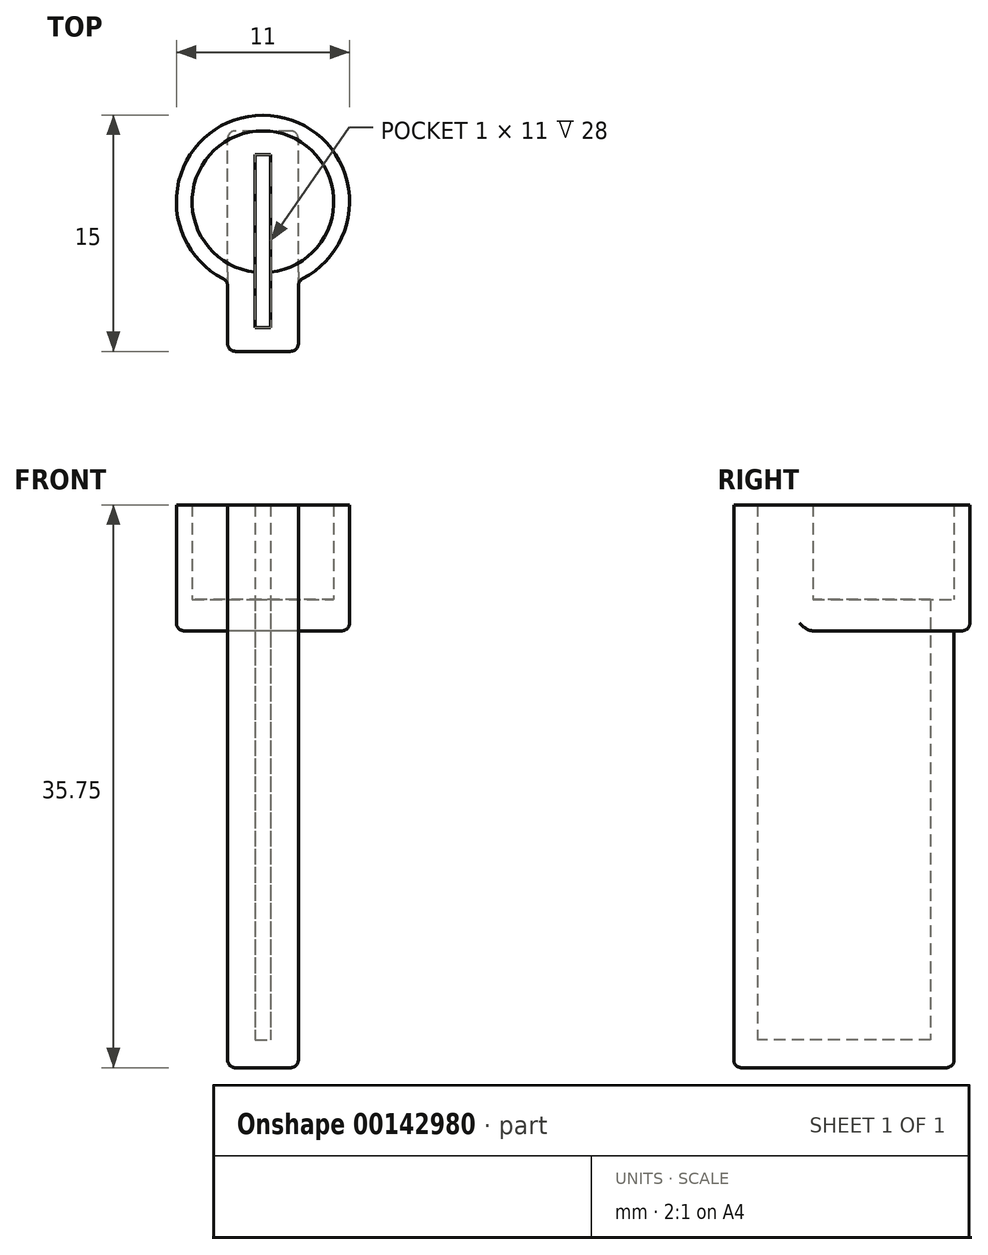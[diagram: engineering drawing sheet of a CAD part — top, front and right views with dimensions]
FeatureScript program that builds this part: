
annotation { "Feature Type Name" : "Feature", "Feature Type Description" : "" }
export const myFeature = defineFeature(function(context is Context, id is Id, definition is map)
    precondition{}
    {
        {
            var Q0;
            Q0=qCreatedBy(makeId("Top.planeOp"),FACE);
            var sketch = newSketch(context, id + "F0", { "sketchPlane" : qUnion([Q0])});
            skLineSegment(sketch, "E0.bottom", {"start": v(2.25, -7) * mm, "end": v(-2.25, -7) * mm});
            skLineSegment(sketch, "E0.top", {"start": v(2.25, 7) * mm, "end": v(-2.25, 7) * mm});
            skLineSegment(sketch, "E0.left", {"start": v(2.25, -7) * mm, "end": v(2.25, 7) * mm});
            skLineSegment(sketch, "E0.right", {"start": v(-2.25, -7) * mm, "end": v(-2.25, 7) * mm});
            skPoint(sketch, "E0.middle", {"position": v(0, 0) * mm});
            skSolve(sketch);
        }
        {
            var Q0;
            Q0 = qSketchRegion(id + "F0", true);
            extrude(context, id + "F1", {"entities" : qUnion([Q0]), "depth" : 1.75 * mm});
        }
        {
            var Q0;
            Q0=makeQuery(id+"F1.opExtrude","CAP_FACE",FACE,{"disambiguationData":[OSD([sQuery(id+"F0.wireOp",EDGE,"E0.bottom"),sQuery(id+"F0.wireOp",EDGE,"E0.top"),sQuery(id+"F0.wireOp",EDGE,"E0.left"),sQuery(id+"F0.wireOp",EDGE,"E0.right")])],"isStart":false});
            var sketch = newSketch(context, id + "F2", { "sketchPlane" : qUnion([Q0])});
            skPoint(sketch, "E1.middle", {"position": v(0, 0) * mm});
            skLineSegment(sketch, "E2.bottom", {"start": v(-2.25, 7) * mm, "end": v(2.25, 7) * mm});
            skLineSegment(sketch, "E2.top", {"start": v(-2.25, -7) * mm, "end": v(2.25, -7) * mm});
            skLineSegment(sketch, "E2.left", {"start": v(-2.25, 7) * mm, "end": v(-2.25, -7) * mm});
            skLineSegment(sketch, "E2.right", {"start": v(2.25, 7) * mm, "end": v(2.25, -7) * mm});
            skLineSegment(sketch, "E3.bottom", {"start": v(-0.5, 5.5) * mm, "end": v(0.5, 5.5) * mm});
            skLineSegment(sketch, "E3.top", {"start": v(-0.5, -5.5) * mm, "end": v(0.5, -5.5) * mm});
            skLineSegment(sketch, "E3.left", {"start": v(-0.5, 5.5) * mm, "end": v(-0.5, -5.5) * mm});
            skLineSegment(sketch, "E3.right", {"start": v(0.5, 5.5) * mm, "end": v(0.5, -5.5) * mm});
            skSolve(sketch);
        }
        {
            var Q0;
            Q0 = qSketchRegion(id + "F2", true);
            extrude(context, id + "F3", {"entities" : qUnion([Q0]), "operationType" : NewBodyOperationType.ADD, "depth" : 26 * mm});
        }
        {
            var Q0;
            Q0=makeQuery(id+"F3.opExtrude","CAP_FACE",FACE,{"disambiguationData":[OSD([sQuery(id+"F2.wireOp",EDGE,"E2.bottom"),sQuery(id+"F2.wireOp",EDGE,"E2.top"),sQuery(id+"F2.wireOp",EDGE,"E2.left"),sQuery(id+"F2.wireOp",EDGE,"E2.right"),sQuery(id+"F2.wireOp",EDGE,"E3.bottom"),sQuery(id+"F2.wireOp",EDGE,"E3.top"),sQuery(id+"F2.wireOp",EDGE,"E3.left"),sQuery(id+"F2.wireOp",EDGE,"E3.right")])],"isStart":false});
            var sketch = newSketch(context, id + "F4", { "sketchPlane" : qUnion([Q0])});
            skPoint(sketch, "E4.first.point", {"position": v(-4.26, 6.2) * mm});
            skPoint(sketch, "E4.second.point", {"position": v(4.05, 6.34) * mm});
            skPoint(sketch, "E4.third.point", {"position": v(3.62, -1.7) * mm});
            skLineSegment(sketch, "E5", {"start": v(-2.25, -2.52) * mm, "end": v(-2.25, -7) * mm});
            skLineSegment(sketch, "E6", {"start": v(-2.25, -7) * mm, "end": v(2.25, -7) * mm});
            skLineSegment(sketch, "E7", {"start": v(2.25, -7) * mm, "end": v(2.25, -2.52) * mm});
            skLineSegment(sketch, "E8", {"start": v(0.5, -2.98) * mm, "end": v(0.5, -5.5) * mm});
            skLineSegment(sketch, "E9", {"start": v(0.5, -5.5) * mm, "end": v(0.5, 5.5) * mm});
            skLineSegment(sketch, "E10", {"start": v(0.5, -5.5) * mm, "end": v(-0.5, -5.5) * mm});
            skLineSegment(sketch, "E11", {"start": v(-0.5, -5.5) * mm, "end": v(-0.5, 5.5) * mm});
            skArc(sketch, "E12.trimOffspring", {"start": v(2.25, -2.52) * mm, "mid": v(0, 8) * mm, "end": v(-2.25, -2.52) * mm});
            skLineSegment(sketch, "E13", {"start": v(-0.5, 5.5) * mm, "end": v(0.5, 5.5) * mm});
            skSolve(sketch);
        }
        {
            var Q0;
            Q0 = qSketchRegion(id + "F4", true);
            extrude(context, id + "F5", {"entities" : qUnion([Q0]), "operationType" : NewBodyOperationType.ADD, "depth" : 2 * mm});
        }
        {
            var Q0;
            Q0=makeQuery(id+"F5.opExtrude","CAP_FACE",FACE,{"disambiguationData":[OSD([sQuery(id+"F4.wireOp",EDGE,"E5"),sQuery(id+"F4.wireOp",EDGE,"E6"),sQuery(id+"F4.wireOp",EDGE,"E7"),sQuery(id+"F4.wireOp",EDGE,"E9"),sQuery(id+"F4.wireOp",EDGE,"E10"),sQuery(id+"F4.wireOp",EDGE,"E11"),sQuery(id+"F4.wireOp",EDGE,"E12.trimOffspring"),sQuery(id+"F4.wireOp",EDGE,"E13")])],"isStart":false});
            var sketch = newSketch(context, id + "F6", { "sketchPlane" : qUnion([Q0])});
            skArc(sketch, "E14", {"start": v(2.25, -2.52) * mm, "mid": v(0, 8) * mm, "end": v(-2.25, -2.52) * mm});
            skArc(sketch, "E15", {"start": v(0.5, -1.97) * mm, "mid": v(0, 7) * mm, "end": v(-0.5, -1.97) * mm});
            skLineSegment(sketch, "E16", {"start": v(-0.5, -1.97) * mm, "end": v(-0.5, -5.5) * mm});
            skLineSegment(sketch, "E17", {"start": v(-0.5, -5.5) * mm, "end": v(0.5, -5.5) * mm});
            skLineSegment(sketch, "E18", {"start": v(0.5, -5.5) * mm, "end": v(0.5, -1.97) * mm});
            skLineSegment(sketch, "E19", {"start": v(-2.25, -2.52) * mm, "end": v(-2.25, -7) * mm});
            skLineSegment(sketch, "E20", {"start": v(-2.25, -7) * mm, "end": v(2.25, -7) * mm});
            skLineSegment(sketch, "E21", {"start": v(2.25, -7) * mm, "end": v(2.25, -2.52) * mm});
            skSolve(sketch);
        }
        {
            var Q0;
            Q0 = qSketchRegion(id + "F6", true);
            extrude(context, id + "F7", {"entities" : qUnion([Q0]), "operationType" : NewBodyOperationType.ADD, "depth" : 6 * mm});
        }
        {
            var Q0;
            Q0=makeQuery(id+"F7.boolean.opBoolean","MERGE",EDGE,{"derivedFrom":[makeQuery(id+"F5.opExtrude","SWEPT_EDGE",EDGE,{"disambiguationData":[OSD([sQuery(id+"F2.wireOp",EDGE,"E2.right"),sQuery(id+"F4.wireOp",EDGE,"E7"),sQuery(id+"F4.wireOp",EDGE,"E12.trimOffspring")])]}),makeQuery(id+"F7.opExtrude","SWEPT_EDGE",EDGE,{"disambiguationData":[OSD([sQuery(id+"F6.wireOp",EDGE,"E14"),sQuery(id+"F6.wireOp",EDGE,"E21")])]})]});
            var Q1;
            Q1=makeQuery(id+"F3.opExtrude","CAP_EDGE",EDGE,{"disambiguationData":[OSD([sQuery(id+"F2.wireOp",EDGE,"E2.right")])],"isStart":false});
            var Q2;
            Q2=makeQuery(id+"F3.opExtrude","CAP_EDGE",EDGE,{"disambiguationData":[OSD([sQuery(id+"F2.wireOp",EDGE,"E2.bottom")])],"isStart":false});
            var Q3;
            Q3=makeQuery(id+"F3.opExtrude","CAP_EDGE",EDGE,{"disambiguationData":[OSD([sQuery(id+"F2.wireOp",EDGE,"E2.left")])],"isStart":false});
            var Q4;
            Q4=makeQuery(id+"F7.boolean.opBoolean","MERGE",EDGE,{"derivedFrom":[makeQuery(id+"F5.opExtrude","SWEPT_EDGE",EDGE,{"disambiguationData":[OSD([sQuery(id+"F2.wireOp",EDGE,"E2.left"),sQuery(id+"F4.wireOp",EDGE,"E5"),sQuery(id+"F4.wireOp",EDGE,"E12.trimOffspring")])]}),makeQuery(id+"F7.opExtrude","SWEPT_EDGE",EDGE,{"disambiguationData":[OSD([sQuery(id+"F6.wireOp",EDGE,"E14"),sQuery(id+"F6.wireOp",EDGE,"E19")])]})]});
            fillet(context, id + "F8", {"entities" : qUnion([Q0, Q1, Q2, Q3, Q4]), "radius" : 0.5 * mm, "tangentPropagation" : true, "allowEdgeOverflow" : false});
        }
        {
            var Q0;
            Q0=makeQuery(id+"F5.opExtrude","CAP_EDGE",EDGE,{"disambiguationData":[OSD([sQuery(id+"F4.wireOp",EDGE,"E12.trimOffspring")])],"isStart":true});
            fillet(context, id + "F9", {"entities" : qUnion([Q0]), "radius" : 0.5 * mm, "tangentPropagation" : true, "allowEdgeOverflow" : false});
        }
        {
            var Q0;
            Q0=makeQuery(id+"F7.boolean.opBoolean","MERGE",EDGE,{"derivedFrom":[makeQuery(id+"F5.boolean.opBoolean","MERGE",EDGE,{"derivedFrom":[makeQuery(id+"F3.boolean.opBoolean","MERGE",EDGE,{"derivedFrom":[makeQuery(id+"F1.opExtrude","SWEPT_EDGE",EDGE,{"disambiguationData":[OSD([sQuery(id+"F0.wireOp",EDGE,"E0.bottom"),sQuery(id+"F0.wireOp",EDGE,"E0.right")])]}),makeQuery(id+"F3.opExtrude","SWEPT_EDGE",EDGE,{"disambiguationData":[OSD([sQuery(id+"F2.wireOp",EDGE,"E2.top"),sQuery(id+"F2.wireOp",EDGE,"E2.left")])]})]}),makeQuery(id+"F5.opExtrude","SWEPT_EDGE",EDGE,{"disambiguationData":[OSD([sQuery(id+"F4.wireOp",EDGE,"E5"),sQuery(id+"F4.wireOp",EDGE,"E6")])]})]}),makeQuery(id+"F7.opExtrude","SWEPT_EDGE",EDGE,{"disambiguationData":[OSD([sQuery(id+"F6.wireOp",EDGE,"E19"),sQuery(id+"F6.wireOp",EDGE,"E20")])]})]});
            var Q1;
            Q1=makeQuery(id+"F7.boolean.opBoolean","MERGE",EDGE,{"derivedFrom":[makeQuery(id+"F5.boolean.opBoolean","MERGE",EDGE,{"derivedFrom":[makeQuery(id+"F3.boolean.opBoolean","MERGE",EDGE,{"derivedFrom":[makeQuery(id+"F1.opExtrude","SWEPT_EDGE",EDGE,{"disambiguationData":[OSD([sQuery(id+"F0.wireOp",EDGE,"E0.bottom"),sQuery(id+"F0.wireOp",EDGE,"E0.left")])]}),makeQuery(id+"F3.opExtrude","SWEPT_EDGE",EDGE,{"disambiguationData":[OSD([sQuery(id+"F2.wireOp",EDGE,"E2.top"),sQuery(id+"F2.wireOp",EDGE,"E2.right")])]})]}),makeQuery(id+"F5.opExtrude","SWEPT_EDGE",EDGE,{"disambiguationData":[OSD([sQuery(id+"F4.wireOp",EDGE,"E6"),sQuery(id+"F4.wireOp",EDGE,"E7")])]})]}),makeQuery(id+"F7.opExtrude","SWEPT_EDGE",EDGE,{"disambiguationData":[OSD([sQuery(id+"F6.wireOp",EDGE,"E20"),sQuery(id+"F6.wireOp",EDGE,"E21")])]})]});
            var Q2;
            Q2=makeQuery(id+"F1.opExtrude","CAP_EDGE",EDGE,{"disambiguationData":[OSD([sQuery(id+"F0.wireOp",EDGE,"E0.bottom")])],"isStart":true});
            var Q3;
            Q3=makeQuery(id+"F1.opExtrude","CAP_EDGE",EDGE,{"disambiguationData":[OSD([sQuery(id+"F0.wireOp",EDGE,"E0.left")])],"isStart":true});
            var Q4;
            Q4=makeQuery(id+"F1.opExtrude","CAP_EDGE",EDGE,{"disambiguationData":[OSD([sQuery(id+"F0.wireOp",EDGE,"E0.right")])],"isStart":true});
            var Q5;
            Q5=makeQuery(id+"F1.opExtrude","CAP_EDGE",EDGE,{"disambiguationData":[OSD([sQuery(id+"F0.wireOp",EDGE,"E0.top")])],"isStart":true});
            var Q6;
            Q6=makeQuery(id+"F3.boolean.opBoolean","MERGE",EDGE,{"derivedFrom":[makeQuery(id+"F1.opExtrude","SWEPT_EDGE",EDGE,{"disambiguationData":[OSD([sQuery(id+"F0.wireOp",EDGE,"E0.top"),sQuery(id+"F0.wireOp",EDGE,"E0.left")])]}),makeQuery(id+"F3.opExtrude","SWEPT_EDGE",EDGE,{"disambiguationData":[OSD([sQuery(id+"F2.wireOp",EDGE,"E2.bottom"),sQuery(id+"F2.wireOp",EDGE,"E2.right")])]})]});
            var Q7;
            Q7=makeQuery(id+"F3.boolean.opBoolean","MERGE",EDGE,{"derivedFrom":[makeQuery(id+"F1.opExtrude","SWEPT_EDGE",EDGE,{"disambiguationData":[OSD([sQuery(id+"F0.wireOp",EDGE,"E0.top"),sQuery(id+"F0.wireOp",EDGE,"E0.right")])]}),makeQuery(id+"F3.opExtrude","SWEPT_EDGE",EDGE,{"disambiguationData":[OSD([sQuery(id+"F2.wireOp",EDGE,"E2.bottom"),sQuery(id+"F2.wireOp",EDGE,"E2.left")])]})]});
            fillet(context, id + "F10", {"entities" : qUnion([Q0, Q1, Q2, Q3, Q4, Q5, Q6, Q7]), "radius" : 0.5 * mm, "tangentPropagation" : true, "allowEdgeOverflow" : false});
        }
    });
